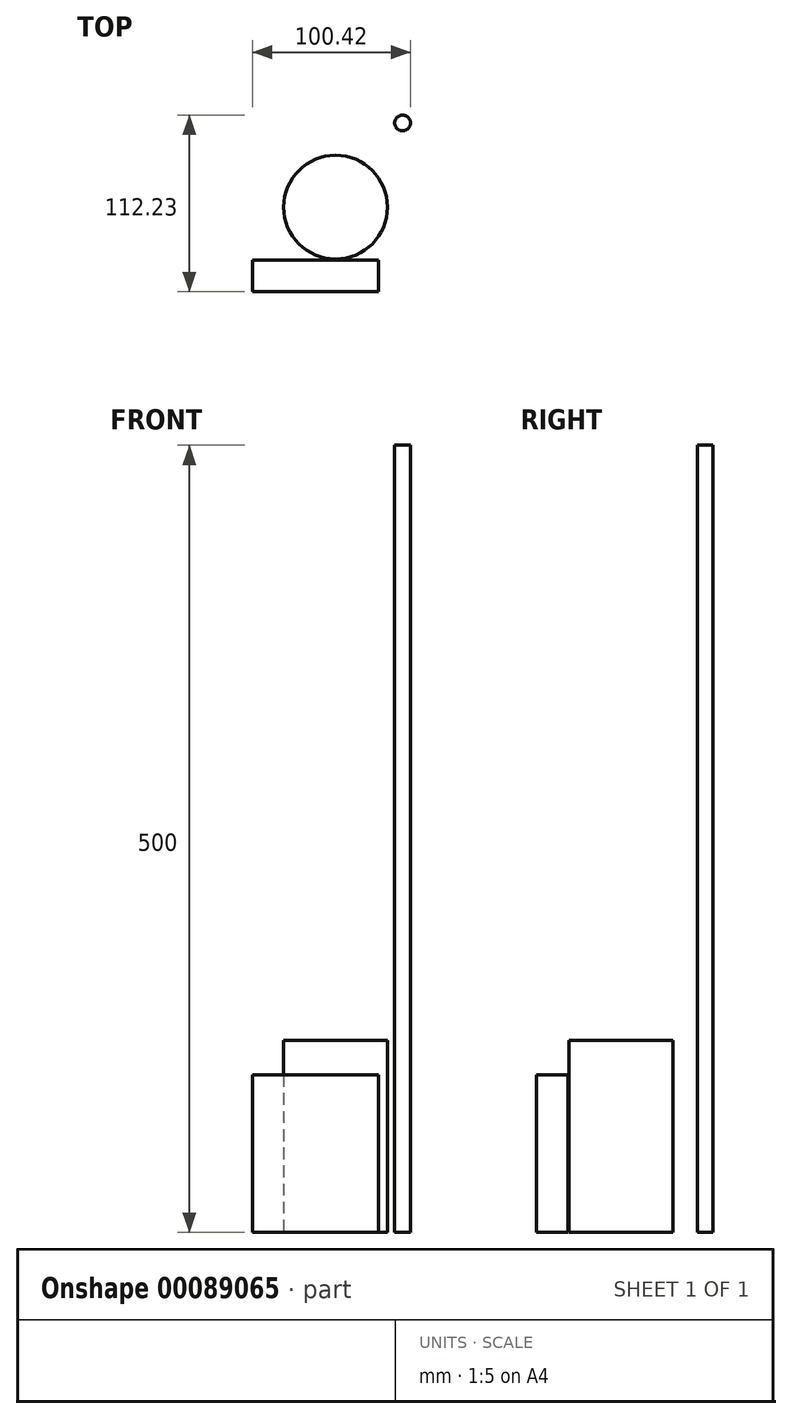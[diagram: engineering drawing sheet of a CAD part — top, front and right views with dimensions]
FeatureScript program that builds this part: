
annotation { "Feature Type Name" : "Feature", "Feature Type Description" : "" }
export const myFeature = defineFeature(function(context is Context, id is Id, definition is map)
    precondition{}
    {
        {
            var Q0;
            Q0=qCreatedBy(makeId("Top.planeOp"),FACE);
            var sketch = newSketch(context, id + "F0", { "sketchPlane" : qUnion([Q0])});
            skCircle(sketch, "E0", {"center": v(0, 0) * mm, "radius": 33 * mm});
            skSolve(sketch);
        }
        {
            var Q0;
            Q0=makeQuery(id+"F0.imprint","IMPRINT",FACE,{"disambiguationData":[TD([[makeQuery(id+"F0.imprint","IMPRINT",EDGE,{"derivedFrom":sQuery(id+"F0.wireOp",EDGE,"E0")}),1.0]])]});
            extrude(context, id + "F1", {"entities" : qUnion([Q0]), "depth" : 122 * mm});
        }
        {
            var Q0;
            Q0=qCreatedBy(makeId("Top.planeOp"),FACE);
            var sketch = newSketch(context, id + "F2", { "sketchPlane" : qUnion([Q0])});
            skCircle(sketch, "E1", {"center": v(42.57, 53.5) * mm, "radius": 5 * mm});
            skSolve(sketch);
        }
        {
            var Q0;
            Q0=makeQuery(id+"F2.imprint","IMPRINT",FACE,{"disambiguationData":[TD([[makeQuery(id+"F2.imprint","IMPRINT",EDGE,{"derivedFrom":sQuery(id+"F2.wireOp",EDGE,"E1")}),1.0]])]});
            extrude(context, id + "F3", {"entities" : qUnion([Q0]), "depth" : 500 * mm});
        }
        {
            var Q0;
            Q0=qCreatedBy(makeId("Top.planeOp"),FACE);
            var sketch = newSketch(context, id + "F4", { "sketchPlane" : qUnion([Q0])});
            skLineSegment(sketch, "E2.bottom", {"start": v(-52.85, -33.73) * mm, "end": v(27.15, -33.73) * mm});
            skLineSegment(sketch, "E2.top", {"start": v(-52.85, -53.73) * mm, "end": v(27.15, -53.73) * mm});
            skLineSegment(sketch, "E2.left", {"start": v(-52.85, -33.73) * mm, "end": v(-52.85, -53.73) * mm});
            skLineSegment(sketch, "E2.right", {"start": v(27.15, -33.73) * mm, "end": v(27.15, -53.73) * mm});
            skSolve(sketch);
        }
        {
            var Q0;
            Q0=makeQuery(id+"F4.imprint","IMPRINT",FACE,{"disambiguationData":[TD([[makeQuery(id+"F4.imprint","IMPRINT",EDGE,{"derivedFrom":sQuery(id+"F4.wireOp",EDGE,"E2.bottom")}),-1.0]])]});
            extrude(context, id + "F5", {"entities" : qUnion([Q0]), "depth" : 100 * mm});
        }
    });
